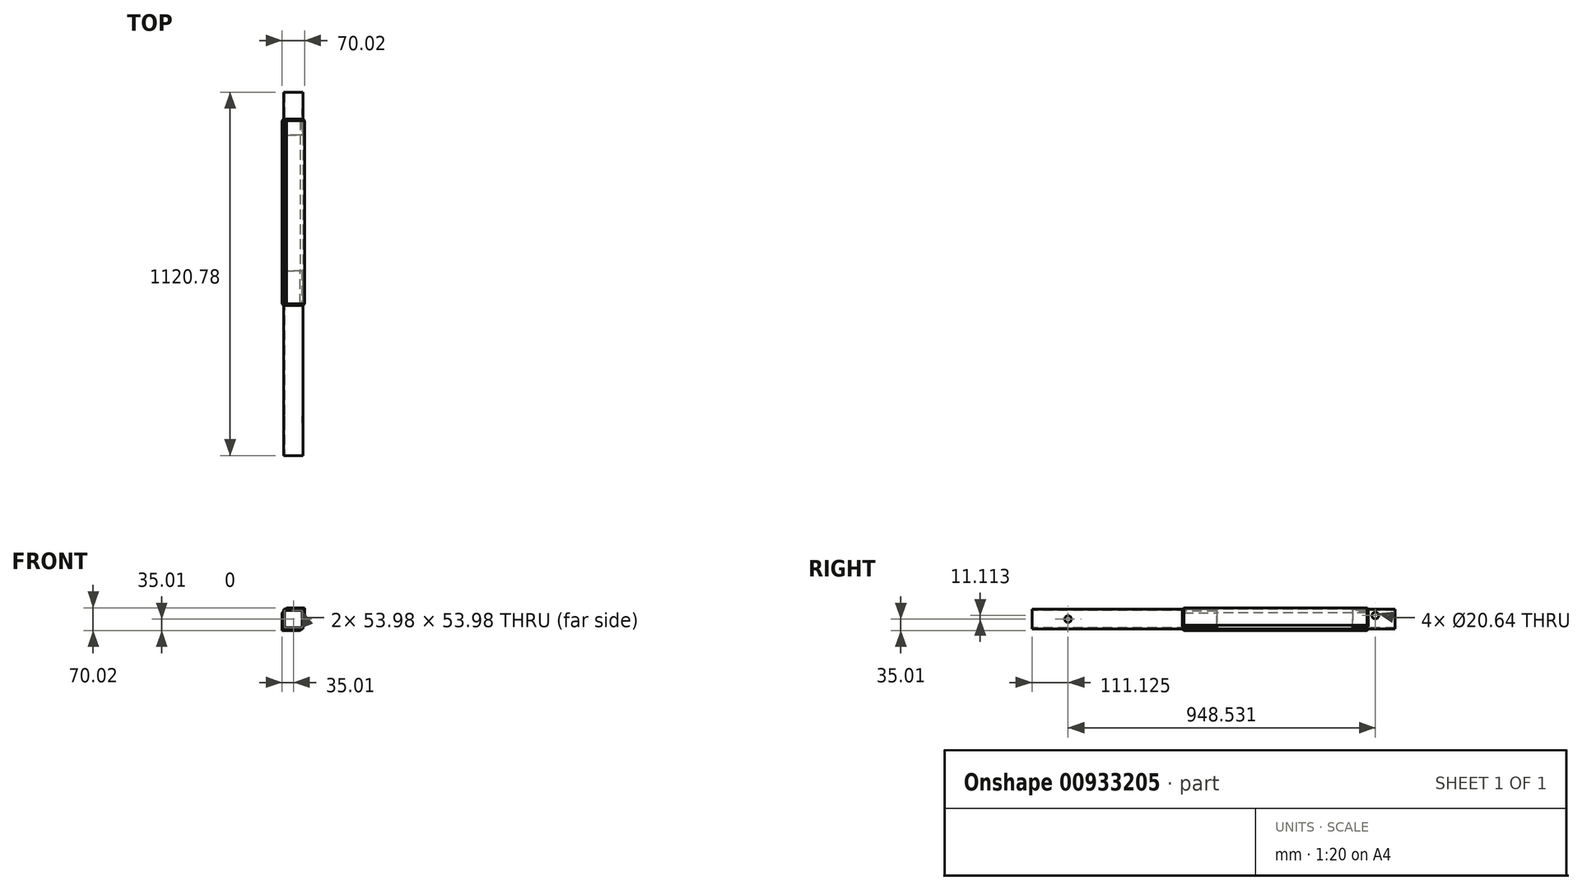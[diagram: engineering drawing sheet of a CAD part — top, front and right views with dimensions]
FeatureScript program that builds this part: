
annotation { "Feature Type Name" : "Feature", "Feature Type Description" : "" }
export const myFeature = defineFeature(function(context is Context, id is Id, definition is map)
    precondition{}
    {
        {
            var Q0;
            Q0=qCreatedBy(makeId("Front.planeOp"),FACE);
            var sketch = newSketch(context, id + "F0", { "sketchPlane" : qUnion([Q0])});
            skLineSegment(sketch, "E0.bottom", {"start": v(26.99, 30.16) * mm, "end": v(-26.99, 30.16) * mm});
            skLineSegment(sketch, "E0.top", {"start": v(26.99, -30.16) * mm, "end": v(-26.99, -30.16) * mm});
            skLineSegment(sketch, "E0.left", {"start": v(30.16, 26.99) * mm, "end": v(30.16, -26.99) * mm});
            skLineSegment(sketch, "E0.right", {"start": v(-30.16, 26.99) * mm, "end": v(-30.16, -26.99) * mm});
            skPoint(sketch, "E0.middle", {"position": v(0, 0) * mm});
            skLineSegment(sketch, "E1.0", {"start": v(23.81, 26.99) * mm, "end": v(-23.81, 26.99) * mm});
            skLineSegment(sketch, "E1.1", {"start": v(26.99, 23.81) * mm, "end": v(26.99, -23.81) * mm});
            skLineSegment(sketch, "E1.2", {"start": v(23.81, -26.99) * mm, "end": v(-23.81, -26.99) * mm});
            skLineSegment(sketch, "E1.3", {"start": v(-26.99, 23.81) * mm, "end": v(-26.99, -23.81) * mm});
            skPoint(sketch, "E2.visualSharp", {"position": v(-26.99, 26.99) * mm});
            skPoint(sketch, "E3.visualSharp", {"position": v(-30.16, 30.16) * mm});
            skPoint(sketch, "E4.visualSharp", {"position": v(30.16, 30.16) * mm});
            skPoint(sketch, "E5.visualSharp", {"position": v(26.99, 26.99) * mm});
            skPoint(sketch, "E6.visualSharp", {"position": v(26.99, -26.99) * mm});
            skPoint(sketch, "E7.visualSharp", {"position": v(30.16, -30.16) * mm});
            skPoint(sketch, "E8.visualSharp", {"position": v(-26.99, -26.99) * mm});
            skPoint(sketch, "E9.visualSharp", {"position": v(-30.16, -30.16) * mm});
            skLineSegment(sketch, "E10", {"start": v(-26.99, -23.81) * mm, "end": v(-26.99, -26.99) * mm});
            skLineSegment(sketch, "E11", {"start": v(-23.81, -26.99) * mm, "end": v(-26.99, -26.99) * mm});
            skLineSegment(sketch, "E12", {"start": v(-30.16, -26.99) * mm, "end": v(-30.16, -30.16) * mm});
            skLineSegment(sketch, "E13", {"start": v(-30.16, -30.16) * mm, "end": v(-26.99, -30.16) * mm});
            skLineSegment(sketch, "E14", {"start": v(26.99, -23.81) * mm, "end": v(26.99, -26.99) * mm});
            skLineSegment(sketch, "E15", {"start": v(26.99, -26.99) * mm, "end": v(23.81, -26.99) * mm});
            skLineSegment(sketch, "E16", {"start": v(30.16, -26.99) * mm, "end": v(30.16, -30.16) * mm});
            skLineSegment(sketch, "E17", {"start": v(26.99, -30.16) * mm, "end": v(30.16, -30.16) * mm});
            skLineSegment(sketch, "E18", {"start": v(26.99, 23.81) * mm, "end": v(26.99, 26.99) * mm});
            skLineSegment(sketch, "E19", {"start": v(26.99, 26.99) * mm, "end": v(23.81, 26.99) * mm});
            skLineSegment(sketch, "E20", {"start": v(30.16, 26.99) * mm, "end": v(30.16, 30.16) * mm});
            skLineSegment(sketch, "E21", {"start": v(26.99, 30.16) * mm, "end": v(30.16, 30.16) * mm});
            skLineSegment(sketch, "E22", {"start": v(-23.81, 26.99) * mm, "end": v(-26.99, 26.99) * mm});
            skLineSegment(sketch, "E23", {"start": v(-26.99, 26.99) * mm, "end": v(-26.99, 23.81) * mm});
            skLineSegment(sketch, "E24", {"start": v(-30.16, 26.99) * mm, "end": v(-30.16, 30.16) * mm});
            skLineSegment(sketch, "E25", {"start": v(-30.16, 30.16) * mm, "end": v(-26.99, 30.16) * mm});
            skSolve(sketch);
        }
        {
            var Q0;
            Q0=makeQuery(id+"F0.imprint","IMPRINT",FACE,{"disambiguationData":[TD([[makeQuery(id+"F0.imprint","IMPRINT",EDGE,{"derivedFrom":sQuery(id+"F0.wireOp",EDGE,"E0.bottom")}),1.0]])]});
            extrude(context, id + "F1", {"entities" : qUnion([Q0]), "oppositeDirection" : true, "depth" : 1120.77 * mm, "offsetDistance" : 25.4 * mm});
        }
        {
            var Q0;
            Q0=qCreatedBy(makeId("Right.planeOp"),FACE);
            var sketch = newSketch(context, id + "F2", { "sketchPlane" : qUnion([Q0])});
            skLineSegment(sketch, "E26", {"start": v(0, 0) * mm, "end": v(569.91, 0) * mm, "construction": true});
            skLineSegment(sketch, "E27", {"start": v(569.91, 0) * mm, "end": v(569.91, -86.32) * mm});
            skLineSegment(sketch, "E28", {"start": v(569.91, -86.32) * mm, "end": v(989.01, -86.32) * mm});
            skLineSegment(sketch, "E29", {"start": v(989.01, -86.32) * mm, "end": v(989.01, 80.05) * mm});
            skLineSegment(sketch, "E30", {"start": v(989.01, 80.05) * mm, "end": v(569.91, 80.05) * mm});
            skLineSegment(sketch, "E31", {"start": v(569.91, 80.05) * mm, "end": v(569.91, 0) * mm});
            skSolve(sketch);
        }
        {
            var Q0;
            Q0 = qSketchRegion(id + "F2", true);
            extrude(context, id + "F3", {"entities" : qUnion([Q0]), "operationType" : NewBodyOperationType.REMOVE, "endBound" : BoundingType.SYMMETRIC, "oppositeDirection" : true, "depth" : 106.68 * mm, "offsetDistance" : 25.4 * mm});
        }
        {
            var Q0;
            Q0=qCreatedBy(makeId("Front.planeOp"),FACE);
            cPlane(context, id + "F4", {"entities" : qUnion([Q0]), "cplaneType" : CPlaneType.OFFSET, "offset" : 468.3 * mm, "oppositeDirection" : true, "width" : 152.4 * mm, "height" : 152.4 * mm});
        }
        {
            var Q0;
            Q0=qCreatedBy(id+"F4.planeOp",FACE);
            var sketch = newSketch(context, id + "F5", { "sketchPlane" : qUnion([Q0])});
            skLineSegment(sketch, "E32", {"start": v(0, 0) * mm, "end": v(0, 30.25) * mm, "construction": true});
            skLineSegment(sketch, "E33", {"start": v(0, 0) * mm, "end": v(30.25, 0) * mm, "construction": true});
            skLineSegment(sketch, "E34", {"start": v(30.25, 0) * mm, "end": v(-20.55, 0) * mm, "construction": true});
            skLineSegment(sketch, "E35", {"start": v(-20.55, 0) * mm, "end": v(-20.55, 30.25) * mm, "construction": true});
            skLineSegment(sketch, "E36", {"start": v(-20.55, 30.25) * mm, "end": v(30.25, 30.25) * mm});
            skLineSegment(sketch, "E37", {"start": v(30.25, 30.25) * mm, "end": v(30.25, -19.03) * mm});
            skLineSegment(sketch, "E38", {"start": v(30.25, -19.03) * mm, "end": v(35.01, -19.03) * mm});
            skLineSegment(sketch, "E39", {"start": v(35.01, -19.03) * mm, "end": v(35.01, 35.01) * mm});
            skLineSegment(sketch, "E40", {"start": v(35.01, 35.01) * mm, "end": v(-20.55, 35.01) * mm});
            skLineSegment(sketch, "E41", {"start": v(-20.55, 35.01) * mm, "end": v(-20.55, 30.25) * mm});
            skLineSegment(sketch, "E42.1.0", {"start": v(-35.01, 19.03) * mm, "end": v(-35.01, -35.01) * mm});
            skLineSegment(sketch, "E42.1.1", {"start": v(-35.01, -35.01) * mm, "end": v(20.55, -35.01) * mm});
            skLineSegment(sketch, "E42.1.2", {"start": v(20.55, -35.01) * mm, "end": v(20.55, -30.25) * mm});
            skLineSegment(sketch, "E42.1.3", {"start": v(20.55, -30.25) * mm, "end": v(-30.25, -30.25) * mm});
            skLineSegment(sketch, "E42.1.4", {"start": v(-30.25, -30.25) * mm, "end": v(-30.25, 19.03) * mm});
            skLineSegment(sketch, "E42.1.5", {"start": v(-30.25, 19.03) * mm, "end": v(-35.01, 19.03) * mm});
            skPoint(sketch, "E42.center", {"position": v(0, 0) * mm});
            skSolve(sketch);
        }
        {
            var Q0;
            Q0=makeQuery(id+"F5.imprint","IMPRINT",FACE,{"disambiguationData":[TD([[makeQuery(id+"F5.imprint","IMPRINT",EDGE,{"derivedFrom":sQuery(id+"F5.wireOp",EDGE,"E36")}),1.0]])]});
            var Q1;
            Q1=makeQuery(id+"F5.imprint","IMPRINT",FACE,{"disambiguationData":[TD([[makeQuery(id+"F5.imprint","IMPRINT",EDGE,{"derivedFrom":sQuery(id+"F5.wireOp",EDGE,"E42.1.0")}),1.0]])]});
            extrude(context, id + "F6", {"entities" : qUnion([Q0, Q1]), "oppositeDirection" : true, "depth" : 565.15 * mm, "offsetDistance" : 25.4 * mm});
        }
        {
            var Q0;
            Q0=makeQuery(id+"F6.opExtrude","SWEPT_FACE",FACE,{"disambiguationData":[OSD([sQuery(id+"F5.wireOp",EDGE,"E41")])]});
            var sketch = newSketch(context, id + "F7", { "sketchPlane" : qUnion([Q0])});
            skLineSegment(sketch, "E43", {"start": v(-468.31, 35.01) * mm, "end": v(-459.42, 26.12) * mm});
            skLineSegment(sketch, "E44", {"start": v(-459.42, 26.12) * mm, "end": v(-468.31, 26.12) * mm});
            skLineSegment(sketch, "E45", {"start": v(-468.31, 26.12) * mm, "end": v(-468.31, 35.01) * mm});
            skLineSegment(sketch, "E46", {"start": v(-1033.46, 35.01) * mm, "end": v(-1033.46, 26.12) * mm});
            skLineSegment(sketch, "E47", {"start": v(-1033.46, 26.12) * mm, "end": v(-1042.35, 26.12) * mm});
            skLineSegment(sketch, "E48", {"start": v(-1042.35, 26.12) * mm, "end": v(-1033.46, 35.01) * mm});
            skSolve(sketch);
        }
        {
            var Q0;
            {var subQ4=sQuery(id+"F7.wireOp",EDGE,"E47");Q0=makeQuery(id+"F7.imprint","IMPRINT",FACE,{"disambiguationData":[TD([[makeQuery(id+"F7.imprint","IMPRINT",EDGE,{"derivedFrom":subQ4}),-1.0]])]});}
            var Q1;
            {var subQ0=sQuery(id+"F7.wireOp",EDGE,"E43");Q1=makeQuery(id+"F7.imprint","IMPRINT",FACE,{"disambiguationData":[TD([[makeQuery(id+"F7.imprint","IMPRINT",EDGE,{"derivedFrom":subQ0}),-1.0]])]});}
            var Q2;
            Q2=makeQuery(id+"F6.opExtrude","SWEPT_FACE",FACE,{"disambiguationData":[OSD([sQuery(id+"F5.wireOp",EDGE,"E39")])]});
            extrude(context, id + "F8", {"entities" : qUnion([Q0, Q1]), "operationType" : NewBodyOperationType.ADD, "endBound" : BoundingType.UP_TO_SURFACE, "oppositeDirection" : true, "depth" : 50.8 * mm, "endBoundEntityFace" : qUnion([Q2]), "offsetDistance" : 25.4 * mm});
        }
        {
            var Q0;
            Q0=makeQuery(id+"F6.opExtrude","SWEPT_FACE",FACE,{"disambiguationData":[OSD([sQuery(id+"F5.wireOp",EDGE,"E38")])]});
            var sketch = newSketch(context, id + "F9", { "sketchPlane" : qUnion([Q0])});
            skLineSegment(sketch, "E49", {"start": v(35.01, -1033.46) * mm, "end": v(26.12, -1033.46) * mm});
            skLineSegment(sketch, "E50", {"start": v(26.12, -1033.46) * mm, "end": v(26.12, -1042.35) * mm});
            skLineSegment(sketch, "E51", {"start": v(26.12, -1042.35) * mm, "end": v(35.01, -1033.46) * mm});
            skLineSegment(sketch, "E52", {"start": v(35.01, -468.31) * mm, "end": v(26.12, -468.31) * mm});
            skLineSegment(sketch, "E53", {"start": v(26.12, -468.31) * mm, "end": v(26.12, -459.42) * mm});
            skLineSegment(sketch, "E54", {"start": v(26.12, -459.42) * mm, "end": v(35.01, -468.31) * mm});
            skSolve(sketch);
        }
        {
            var Q0;
            {var subQ4=sQuery(id+"F9.wireOp",EDGE,"E53");Q0=makeQuery(id+"F9.imprint","IMPRINT",FACE,{"disambiguationData":[TD([[makeQuery(id+"F9.imprint","IMPRINT",EDGE,{"derivedFrom":subQ4}),-1.0]])]});}
            var Q1;
            {var subQ4=sQuery(id+"F9.wireOp",EDGE,"E50");Q1=makeQuery(id+"F9.imprint","IMPRINT",FACE,{"disambiguationData":[TD([[makeQuery(id+"F9.imprint","IMPRINT",EDGE,{"derivedFrom":subQ4}),1.0]])]});}
            var Q2;
            Q2=makeQuery(id+"F8.opExtrude","SWEPT_FACE",FACE,{"disambiguationData":[OSD([sQuery(id+"F7.wireOp",EDGE,"E47")])]});
            extrude(context, id + "F10", {"entities" : qUnion([Q0, Q1]), "operationType" : NewBodyOperationType.ADD, "endBound" : BoundingType.UP_TO_SURFACE, "oppositeDirection" : true, "depth" : 25.4 * mm, "endBoundEntityFace" : qUnion([Q2]), "offsetDistance" : 25.4 * mm});
        }
        {
            var Q0;
            {var subQ3=sQuery(id+"F7.wireOp",EDGE,"E44");Q0=makeQuery(id+"F8.boolean.opBoolean","SPLIT",FACE,{"disambiguationData":[TD([makeQuery(id+"F1.opExtrude","SWEPT_FACE",FACE,{"disambiguationData":[OSD([sQuery(id+"F0.wireOp",EDGE,"E0.left")])]})])],"derivedFrom":makeQuery(id+"F8.opExtrude","SWEPT_FACE",FACE,{"disambiguationData":[OSD([subQ3])]})});}
            var sketch = newSketch(context, id + "F11", { "sketchPlane" : qUnion([Q0])});
            skLineSegment(sketch, "E55", {"start": v(30.16, -459.42) * mm, "end": v(35.01, -459.42) * mm});
            skLineSegment(sketch, "E56", {"start": v(35.01, -459.42) * mm, "end": v(35.01, -468.31) * mm});
            skLineSegment(sketch, "E57", {"start": v(35.01, -468.31) * mm, "end": v(30.16, -463.46) * mm});
            skLineSegment(sketch, "E58", {"start": v(30.16, -463.46) * mm, "end": v(30.16, -459.42) * mm});
            skSolve(sketch);
        }
        {
            var Q0;
            Q0 = qSketchRegion(id + "F11", true);
            extrude(context, id + "F12", {"entities" : qUnion([Q0]), "operationType" : NewBodyOperationType.REMOVE, "oppositeDirection" : true, "depth" : 25.4 * mm, "offsetDistance" : 25.4 * mm});
        }
        {
            var Q0;
            {var subQ1=sQuery(id+"F5.wireOp",EDGE,"E37");var subQ4=sQuery(id+"F7.wireOp",EDGE,"E47");Q0=makeQuery(id+"F8.boolean.opBoolean","SPLIT",FACE,{"disambiguationData":[TD([makeQuery(id+"F6.opExtrude","SWEPT_FACE",FACE,{"disambiguationData":[OSD([subQ1])]})])],"derivedFrom":makeQuery(id+"F8.opExtrude","SWEPT_FACE",FACE,{"disambiguationData":[OSD([subQ4])]})});}
            var sketch = newSketch(context, id + "F13", { "sketchPlane" : qUnion([Q0])});
            skLineSegment(sketch, "E59", {"start": v(35.01, -1033.46) * mm, "end": v(30.16, -1038.31) * mm});
            skLineSegment(sketch, "E60", {"start": v(30.16, -1038.31) * mm, "end": v(30.16, -1042.35) * mm});
            skLineSegment(sketch, "E61", {"start": v(30.16, -1042.35) * mm, "end": v(35.01, -1042.35) * mm});
            skLineSegment(sketch, "E62", {"start": v(35.01, -1042.35) * mm, "end": v(35.01, -1033.46) * mm});
            skSolve(sketch);
        }
        {
            var Q0;
            Q0 = qSketchRegion(id + "F13", true);
            extrude(context, id + "F14", {"entities" : qUnion([Q0]), "operationType" : NewBodyOperationType.REMOVE, "oppositeDirection" : true, "depth" : 25.4 * mm, "offsetDistance" : 25.4 * mm});
        }
        {
            var Q0;
            Q0=makeQuery(id+"F6.opExtrude","SWEPT_FACE",FACE,{"disambiguationData":[OSD([sQuery(id+"F5.wireOp",EDGE,"E42.1.2")])]});
            var sketch = newSketch(context, id + "F15", { "sketchPlane" : qUnion([Q0])});
            skLineSegment(sketch, "E63", {"start": v(468.31, -35.01) * mm, "end": v(468.31, -26.12) * mm});
            skLineSegment(sketch, "E64", {"start": v(468.31, -26.12) * mm, "end": v(459.42, -26.12) * mm});
            skLineSegment(sketch, "E65", {"start": v(459.42, -26.12) * mm, "end": v(468.31, -35.01) * mm});
            skLineSegment(sketch, "E66", {"start": v(1033.46, -35.01) * mm, "end": v(1033.46, -26.12) * mm});
            skLineSegment(sketch, "E67", {"start": v(1033.46, -26.12) * mm, "end": v(1042.35, -26.12) * mm});
            skLineSegment(sketch, "E68", {"start": v(1042.35, -26.12) * mm, "end": v(1033.46, -35.01) * mm});
            skSolve(sketch);
        }
        {
            var Q0;
            Q0 = qSketchRegion(id + "F15", true);
            var Q1;
            Q1=makeQuery(id+"F6.opExtrude","SWEPT_FACE",FACE,{"disambiguationData":[OSD([sQuery(id+"F5.wireOp",EDGE,"E42.1.0")])]});
            extrude(context, id + "F16", {"entities" : qUnion([Q0]), "operationType" : NewBodyOperationType.ADD, "endBound" : BoundingType.UP_TO_SURFACE, "oppositeDirection" : true, "depth" : 25.4 * mm, "endBoundEntityFace" : qUnion([Q1]), "offsetDistance" : 25.4 * mm});
        }
        {
            var Q0;
            Q0=makeQuery(id+"F6.opExtrude","SWEPT_FACE",FACE,{"disambiguationData":[OSD([sQuery(id+"F5.wireOp",EDGE,"E42.1.5")])]});
            var sketch = newSketch(context, id + "F17", { "sketchPlane" : qUnion([Q0])});
            skLineSegment(sketch, "E69", {"start": v(-35.01, 468.31) * mm, "end": v(-26.12, 468.31) * mm});
            skLineSegment(sketch, "E70", {"start": v(-26.12, 468.31) * mm, "end": v(-26.12, 459.42) * mm});
            skLineSegment(sketch, "E71", {"start": v(-26.12, 459.42) * mm, "end": v(-35.01, 468.31) * mm});
            skLineSegment(sketch, "E72", {"start": v(-35.01, 1033.46) * mm, "end": v(-26.12, 1033.46) * mm});
            skLineSegment(sketch, "E73", {"start": v(-26.12, 1033.46) * mm, "end": v(-26.12, 1042.35) * mm});
            skLineSegment(sketch, "E74", {"start": v(-26.12, 1042.35) * mm, "end": v(-35.01, 1033.46) * mm});
            skSolve(sketch);
        }
        {
            var Q0;
            Q0 = qSketchRegion(id + "F17", true);
            var Q1;
            {var subQ2=sQuery(id+"F0.wireOp",EDGE,"E17");var subQ4=sQuery(id+"F0.wireOp",EDGE,"E13");var subQ8=sQuery(id+"F0.wireOp",EDGE,"E0.top");Q1=makeQuery(id+"F3.boolean.opBoolean","SPLIT",FACE,{"disambiguationData":[TD([makeQuery(id+"F3.opExtrude","SWEPT_FACE",FACE,{"disambiguationData":[OSD([sQuery(id+"F2.wireOp",EDGE,"E27"),sQuery(id+"F2.wireOp",EDGE,"E31")])]})])],"derivedFrom":makeQuery(id+"F1.opExtrude","SWEPT_FACE",FACE,{"disambiguationData":[OSD([subQ8,subQ4,subQ2])]})});}
            extrude(context, id + "F18", {"entities" : qUnion([Q0]), "operationType" : NewBodyOperationType.ADD, "endBound" : BoundingType.UP_TO_SURFACE, "oppositeDirection" : true, "depth" : 50.8 * mm, "endBoundEntityFace" : qUnion([Q1]), "offsetDistance" : 25.4 * mm});
        }
        {
            var Q0;
            {var subQ1=sQuery(id+"F5.wireOp",EDGE,"E42.1.0");var subQ3=sQuery(id+"F15.wireOp",EDGE,"E67");Q0=makeQuery(id+"F16.boolean.opBoolean","SPLIT",FACE,{"disambiguationData":[TD([makeQuery(id+"F6.opExtrude","SWEPT_FACE",FACE,{"disambiguationData":[OSD([subQ1])]})])],"derivedFrom":makeQuery(id+"F16.opExtrude","SWEPT_FACE",FACE,{"disambiguationData":[OSD([subQ3])]})});}
            var sketch = newSketch(context, id + "F19", { "sketchPlane" : qUnion([Q0])});
            skLineSegment(sketch, "E75", {"start": v(-30.16, 1038.31) * mm, "end": v(-30.16, 1042.35) * mm});
            skLineSegment(sketch, "E76", {"start": v(-30.16, 1042.35) * mm, "end": v(-35.01, 1042.35) * mm});
            skLineSegment(sketch, "E77", {"start": v(-35.01, 1042.35) * mm, "end": v(-35.01, 1033.46) * mm});
            skLineSegment(sketch, "E78", {"start": v(-35.01, 1033.46) * mm, "end": v(-30.16, 1038.31) * mm});
            skSolve(sketch);
        }
        {
            var Q0;
            Q0 = qSketchRegion(id + "F19", true);
            extrude(context, id + "F20", {"entities" : qUnion([Q0]), "operationType" : NewBodyOperationType.REMOVE, "oppositeDirection" : true, "depth" : 25.4 * mm, "offsetDistance" : 25.4 * mm});
        }
        {
            var Q0;
            Q0=makeQuery(id+"F3.boolean.opBoolean","COPY",FACE,{"derivedFrom":makeQuery(id+"F3.opExtrude","SWEPT_FACE",FACE,{"disambiguationData":[OSD([sQuery(id+"F2.wireOp",EDGE,"E27"),sQuery(id+"F2.wireOp",EDGE,"E31")])]})});
            var sketch = newSketch(context, id + "F21", { "sketchPlane" : qUnion([Q0])});
            skLineSegment(sketch, "E79", {"start": v(20.55, 35.01) * mm, "end": v(20.55, 26.12) * mm});
            skLineSegment(sketch, "E80", {"start": v(20.55, 26.12) * mm, "end": v(29.44, 26.12) * mm});
            skLineSegment(sketch, "E81", {"start": v(29.44, 26.12) * mm, "end": v(20.55, 35.01) * mm});
            skLineSegment(sketch, "E82", {"start": v(26.12, 27.92) * mm, "end": v(26.12, 19.03) * mm});
            skLineSegment(sketch, "E83", {"start": v(26.12, 19.03) * mm, "end": v(35.01, 19.03) * mm});
            skLineSegment(sketch, "E84", {"start": v(35.01, 19.03) * mm, "end": v(26.12, 27.92) * mm});
            skLineSegment(sketch, "E85", {"start": v(-26.12, -19.03) * mm, "end": v(-26.12, -27.92) * mm});
            skLineSegment(sketch, "E86", {"start": v(-26.12, -19.03) * mm, "end": v(-35.01, -19.03) * mm});
            skLineSegment(sketch, "E87", {"start": v(-35.01, -19.03) * mm, "end": v(-26.12, -27.92) * mm});
            skLineSegment(sketch, "E88", {"start": v(-20.55, -26.12) * mm, "end": v(-20.55, -35.01) * mm});
            skLineSegment(sketch, "E89", {"start": v(-20.55, -35.01) * mm, "end": v(-29.44, -26.12) * mm});
            skLineSegment(sketch, "E90", {"start": v(-29.44, -26.12) * mm, "end": v(-20.55, -26.12) * mm});
            skSolve(sketch);
        }
        {
            var Q0;
            Q0 = qSketchRegion(id + "F21", true);
            extrude(context, id + "F22", {"entities" : qUnion([Q0]), "operationType" : NewBodyOperationType.ADD, "oppositeDirection" : true, "depth" : 113.8 * mm, "offsetDistance" : 25.4 * mm});
        }
        {
            var Q0;
            {var subQ0=sQuery(id+"F21.wireOp",EDGE,"E89");var subQ1=sQuery(id+"F21.wireOp",EDGE,"E88");Q0=makeQuery(id+"F22.boolean.opBoolean","SPLIT",FACE,{"disambiguationData":[TD([makeQuery(id+"F1.opExtrude","SWEPT_FACE",FACE,{"disambiguationData":[OSD([sQuery(id+"F0.wireOp",EDGE,"E0.top"),sQuery(id+"F0.wireOp",EDGE,"E13"),sQuery(id+"F0.wireOp",EDGE,"E17")])]}),makeQuery(id+"F6.opExtrude","SWEPT_FACE",FACE,{"disambiguationData":[OSD([sQuery(id+"F5.wireOp",EDGE,"E42.1.1")])]}),makeQuery(id+"F16.opExtrude","SWEPT_FACE",FACE,{"disambiguationData":[OSD([sQuery(id+"F15.wireOp",EDGE,"E65")])]}),makeQuery(id+"F22.opExtrude","CAP_FACE",FACE,{"disambiguationData":[OSD([sQuery(id+"F21.wireOp",EDGE,"E85"),sQuery(id+"F21.wireOp",EDGE,"E86"),sQuery(id+"F21.wireOp",EDGE,"E87"),subQ1,subQ0,sQuery(id+"F21.wireOp",EDGE,"E90")])],"isStart":false}),makeQuery(id+"F22.opExtrude","SWEPT_FACE",FACE,{"disambiguationData":[OSD([subQ0])]})])],"derivedFrom":makeQuery(id+"F22.opExtrude","SWEPT_FACE",FACE,{"disambiguationData":[OSD([subQ1])]})});}
            var sketch = newSketch(context, id + "F23", { "sketchPlane" : qUnion([Q0])});
            skLineSegment(sketch, "E91", {"start": v(-456.12, -35.01) * mm, "end": v(-468.31, -35.01) * mm});
            skLineSegment(sketch, "E92", {"start": v(-468.31, -35.01) * mm, "end": v(-463.46, -30.16) * mm});
            skLineSegment(sketch, "E93", {"start": v(-463.46, -30.16) * mm, "end": v(-456.12, -30.16) * mm});
            skLineSegment(sketch, "E94", {"start": v(-456.12, -30.16) * mm, "end": v(-456.12, -35.01) * mm});
            skSolve(sketch);
        }
        {
            var Q0;
            Q0 = qSketchRegion(id + "F23", true);
            extrude(context, id + "F24", {"entities" : qUnion([Q0]), "operationType" : NewBodyOperationType.REMOVE, "oppositeDirection" : true, "depth" : 25.4 * mm, "offsetDistance" : 25.4 * mm});
        }
        {
            var Q0;
            {var subQ0=sQuery(id+"F21.wireOp",EDGE,"E87");var subQ1=sQuery(id+"F21.wireOp",EDGE,"E86");Q0=makeQuery(id+"F22.boolean.opBoolean","SPLIT",FACE,{"disambiguationData":[TD([makeQuery(id+"F1.opExtrude","SWEPT_FACE",FACE,{"disambiguationData":[OSD([sQuery(id+"F0.wireOp",EDGE,"E0.left"),sQuery(id+"F0.wireOp",EDGE,"E16"),sQuery(id+"F0.wireOp",EDGE,"E20")])]}),makeQuery(id+"F6.opExtrude","SWEPT_FACE",FACE,{"disambiguationData":[OSD([sQuery(id+"F5.wireOp",EDGE,"E39")])]}),makeQuery(id+"F8.opExtrude","CAP_FACE",FACE,{"disambiguationData":[OSD([sQuery(id+"F7.wireOp",EDGE,"E43"),sQuery(id+"F7.wireOp",EDGE,"E44"),sQuery(id+"F7.wireOp",EDGE,"E45")])],"isStart":false}),makeQuery(id+"F8.opExtrude","CAP_FACE",FACE,{"disambiguationData":[OSD([sQuery(id+"F7.wireOp",EDGE,"E46"),sQuery(id+"F7.wireOp",EDGE,"E47"),sQuery(id+"F7.wireOp",EDGE,"E48")])],"isStart":false}),makeQuery(id+"F10.opExtrude","SWEPT_FACE",FACE,{"disambiguationData":[OSD([sQuery(id+"F9.wireOp",EDGE,"E54")])]}),makeQuery(id+"F22.opExtrude","CAP_FACE",FACE,{"disambiguationData":[OSD([sQuery(id+"F21.wireOp",EDGE,"E85"),subQ1,subQ0,sQuery(id+"F21.wireOp",EDGE,"E88"),sQuery(id+"F21.wireOp",EDGE,"E89"),sQuery(id+"F21.wireOp",EDGE,"E90")])],"isStart":false}),makeQuery(id+"F22.opExtrude","SWEPT_FACE",FACE,{"disambiguationData":[OSD([subQ0])]})])],"derivedFrom":makeQuery(id+"F22.opExtrude","SWEPT_FACE",FACE,{"disambiguationData":[OSD([subQ1])]})});}
            var sketch = newSketch(context, id + "F25", { "sketchPlane" : qUnion([Q0])});
            skLineSegment(sketch, "E95", {"start": v(30.16, 463.46) * mm, "end": v(30.16, 456.12) * mm});
            skLineSegment(sketch, "E96", {"start": v(30.16, 456.12) * mm, "end": v(35.01, 456.12) * mm});
            skLineSegment(sketch, "E97", {"start": v(35.01, 456.12) * mm, "end": v(35.01, 468.31) * mm});
            skLineSegment(sketch, "E98", {"start": v(35.01, 468.31) * mm, "end": v(30.16, 463.46) * mm});
            skSolve(sketch);
        }
        {
            var Q0;
            Q0 = qSketchRegion(id + "F25", true);
            extrude(context, id + "F26", {"entities" : qUnion([Q0]), "operationType" : NewBodyOperationType.REMOVE, "oppositeDirection" : true, "depth" : 25.4 * mm, "offsetDistance" : 25.4 * mm});
        }
        {
            var Q0;
            {var subQ0=sQuery(id+"F21.wireOp",EDGE,"E81");var subQ1=sQuery(id+"F21.wireOp",EDGE,"E79");Q0=makeQuery(id+"F22.boolean.opBoolean","SPLIT",FACE,{"disambiguationData":[TD([makeQuery(id+"F1.opExtrude","SWEPT_FACE",FACE,{"disambiguationData":[OSD([sQuery(id+"F0.wireOp",EDGE,"E0.bottom"),sQuery(id+"F0.wireOp",EDGE,"E21"),sQuery(id+"F0.wireOp",EDGE,"E25")])]}),makeQuery(id+"F6.opExtrude","SWEPT_FACE",FACE,{"disambiguationData":[OSD([sQuery(id+"F5.wireOp",EDGE,"E40")])]}),makeQuery(id+"F8.opExtrude","SWEPT_FACE",FACE,{"disambiguationData":[OSD([sQuery(id+"F7.wireOp",EDGE,"E43")])]}),makeQuery(id+"F22.opExtrude","CAP_FACE",FACE,{"disambiguationData":[OSD([subQ1,sQuery(id+"F21.wireOp",EDGE,"E80"),subQ0,sQuery(id+"F21.wireOp",EDGE,"E82"),sQuery(id+"F21.wireOp",EDGE,"E83"),sQuery(id+"F21.wireOp",EDGE,"E84")])],"isStart":false}),makeQuery(id+"F22.opExtrude","SWEPT_FACE",FACE,{"disambiguationData":[OSD([subQ0])]})])],"derivedFrom":makeQuery(id+"F22.opExtrude","SWEPT_FACE",FACE,{"disambiguationData":[OSD([subQ1])]})});}
            var sketch = newSketch(context, id + "F27", { "sketchPlane" : qUnion([Q0])});
            skLineSegment(sketch, "E99", {"start": v(456.12, 30.16) * mm, "end": v(456.12, 35.01) * mm});
            skLineSegment(sketch, "E100", {"start": v(456.12, 35.01) * mm, "end": v(468.31, 35.01) * mm});
            skLineSegment(sketch, "E101", {"start": v(468.31, 35.01) * mm, "end": v(463.46, 30.16) * mm});
            skLineSegment(sketch, "E102", {"start": v(463.46, 30.16) * mm, "end": v(456.12, 30.16) * mm});
            skSolve(sketch);
        }
        {
            var Q0;
            Q0 = qSketchRegion(id + "F27", true);
            extrude(context, id + "F28", {"entities" : qUnion([Q0]), "operationType" : NewBodyOperationType.REMOVE, "oppositeDirection" : true, "depth" : 25.4 * mm, "offsetDistance" : 25.4 * mm});
        }
        {
            var Q0;
            {var subQ0=sQuery(id+"F21.wireOp",EDGE,"E84");var subQ1=sQuery(id+"F21.wireOp",EDGE,"E83");Q0=makeQuery(id+"F22.boolean.opBoolean","SPLIT",FACE,{"disambiguationData":[TD([makeQuery(id+"F1.opExtrude","SWEPT_FACE",FACE,{"disambiguationData":[OSD([sQuery(id+"F0.wireOp",EDGE,"E0.right"),sQuery(id+"F0.wireOp",EDGE,"E12"),sQuery(id+"F0.wireOp",EDGE,"E24")])]}),makeQuery(id+"F6.opExtrude","SWEPT_FACE",FACE,{"disambiguationData":[OSD([sQuery(id+"F5.wireOp",EDGE,"E42.1.0")])]}),makeQuery(id+"F16.opExtrude","CAP_FACE",FACE,{"disambiguationData":[OSD([sQuery(id+"F15.wireOp",EDGE,"E63"),sQuery(id+"F15.wireOp",EDGE,"E64"),sQuery(id+"F15.wireOp",EDGE,"E65")])],"isStart":false}),makeQuery(id+"F16.opExtrude","CAP_FACE",FACE,{"disambiguationData":[OSD([sQuery(id+"F15.wireOp",EDGE,"E66"),sQuery(id+"F15.wireOp",EDGE,"E67"),sQuery(id+"F15.wireOp",EDGE,"E68")])],"isStart":false}),makeQuery(id+"F18.opExtrude","SWEPT_FACE",FACE,{"disambiguationData":[OSD([sQuery(id+"F17.wireOp",EDGE,"E71")])]}),makeQuery(id+"F22.opExtrude","CAP_FACE",FACE,{"disambiguationData":[OSD([sQuery(id+"F21.wireOp",EDGE,"E79"),sQuery(id+"F21.wireOp",EDGE,"E80"),sQuery(id+"F21.wireOp",EDGE,"E81"),sQuery(id+"F21.wireOp",EDGE,"E82"),subQ1,subQ0])],"isStart":false}),makeQuery(id+"F22.opExtrude","SWEPT_FACE",FACE,{"disambiguationData":[OSD([subQ0])]})])],"derivedFrom":makeQuery(id+"F22.opExtrude","SWEPT_FACE",FACE,{"disambiguationData":[OSD([subQ1])]})});}
            var sketch = newSketch(context, id + "F29", { "sketchPlane" : qUnion([Q0])});
            skLineSegment(sketch, "E103", {"start": v(-30.16, -463.46) * mm, "end": v(-30.16, -456.12) * mm});
            skLineSegment(sketch, "E104", {"start": v(-30.16, -456.12) * mm, "end": v(-35.01, -456.12) * mm});
            skLineSegment(sketch, "E105", {"start": v(-35.01, -456.12) * mm, "end": v(-35.01, -468.31) * mm});
            skLineSegment(sketch, "E106", {"start": v(-35.01, -468.31) * mm, "end": v(-30.16, -463.46) * mm});
            skSolve(sketch);
        }
        {
            var Q0;
            Q0 = qSketchRegion(id + "F29", true);
            extrude(context, id + "F30", {"entities" : qUnion([Q0]), "operationType" : NewBodyOperationType.REMOVE, "endBound" : BoundingType.SYMMETRIC, "oppositeDirection" : true, "depth" : 508 * mm, "offsetDistance" : 25.4 * mm});
        }
        {
            var Q0;
            Q0=makeQuery(id+"F3.boolean.opBoolean","COPY",FACE,{"derivedFrom":makeQuery(id+"F3.opExtrude","SWEPT_FACE",FACE,{"disambiguationData":[OSD([sQuery(id+"F2.wireOp",EDGE,"E29")])]})});
            var sketch = newSketch(context, id + "F31", { "sketchPlane" : qUnion([Q0])});
            skLineSegment(sketch, "E107", {"start": v(-26.12, 19.03) * mm, "end": v(-35.01, 19.03) * mm});
            skLineSegment(sketch, "E108", {"start": v(-26.12, 19.03) * mm, "end": v(-26.12, 27.92) * mm});
            skLineSegment(sketch, "E109", {"start": v(-26.12, 27.92) * mm, "end": v(-35.01, 19.03) * mm});
            skLineSegment(sketch, "E110", {"start": v(-20.55, 26.12) * mm, "end": v(-29.44, 26.12) * mm});
            skLineSegment(sketch, "E111", {"start": v(-20.55, 26.12) * mm, "end": v(-20.55, 35.01) * mm});
            skLineSegment(sketch, "E112", {"start": v(-20.55, 35.01) * mm, "end": v(-29.44, 26.12) * mm});
            skLineSegment(sketch, "E113", {"start": v(20.55, -35.01) * mm, "end": v(20.55, -26.12) * mm});
            skLineSegment(sketch, "E114", {"start": v(20.55, -26.12) * mm, "end": v(29.44, -26.12) * mm});
            skLineSegment(sketch, "E115", {"start": v(29.44, -26.12) * mm, "end": v(20.55, -35.01) * mm});
            skLineSegment(sketch, "E116", {"start": v(26.12, -19.03) * mm, "end": v(26.12, -27.92) * mm});
            skLineSegment(sketch, "E117", {"start": v(26.12, -19.03) * mm, "end": v(35.01, -19.03) * mm});
            skLineSegment(sketch, "E118", {"start": v(35.01, -19.03) * mm, "end": v(26.12, -27.92) * mm});
            skSolve(sketch);
        }
        {
            var Q0;
            Q0 = qSketchRegion(id + "F31", true);
            extrude(context, id + "F32", {"entities" : qUnion([Q0]), "operationType" : NewBodyOperationType.ADD, "oppositeDirection" : true, "depth" : 63.5 * mm, "offsetDistance" : 25.4 * mm});
        }
        {
            var Q0;
            {var subQ0=sQuery(id+"F31.wireOp",EDGE,"E115");var subQ1=sQuery(id+"F31.wireOp",EDGE,"E113");Q0=makeQuery(id+"F32.boolean.opBoolean","SPLIT",FACE,{"disambiguationData":[TD([makeQuery(id+"F1.opExtrude","SWEPT_FACE",FACE,{"disambiguationData":[OSD([sQuery(id+"F0.wireOp",EDGE,"E0.top"),sQuery(id+"F0.wireOp",EDGE,"E13"),sQuery(id+"F0.wireOp",EDGE,"E17")])]}),makeQuery(id+"F6.opExtrude","SWEPT_FACE",FACE,{"disambiguationData":[OSD([sQuery(id+"F5.wireOp",EDGE,"E42.1.1")])]}),makeQuery(id+"F16.opExtrude","SWEPT_FACE",FACE,{"disambiguationData":[OSD([sQuery(id+"F15.wireOp",EDGE,"E68")])]}),makeQuery(id+"F32.opExtrude","CAP_FACE",FACE,{"disambiguationData":[OSD([subQ1,sQuery(id+"F31.wireOp",EDGE,"E114"),subQ0,sQuery(id+"F31.wireOp",EDGE,"E116"),sQuery(id+"F31.wireOp",EDGE,"E117"),sQuery(id+"F31.wireOp",EDGE,"E118")])],"isStart":false}),makeQuery(id+"F32.opExtrude","SWEPT_FACE",FACE,{"disambiguationData":[OSD([subQ0])]})])],"derivedFrom":makeQuery(id+"F32.opExtrude","SWEPT_FACE",FACE,{"disambiguationData":[OSD([subQ1])]})});}
            var sketch = newSketch(context, id + "F33", { "sketchPlane" : qUnion([Q0])});
            skLineSegment(sketch, "E119", {"start": v(-1033.46, -35.01) * mm, "end": v(-1038.31, -30.16) * mm});
            skLineSegment(sketch, "E120", {"start": v(-1038.31, -30.16) * mm, "end": v(-1052.51, -30.16) * mm});
            skLineSegment(sketch, "E121", {"start": v(-1052.51, -30.16) * mm, "end": v(-1052.51, -35.01) * mm});
            skLineSegment(sketch, "E122", {"start": v(-1052.51, -35.01) * mm, "end": v(-1033.46, -35.01) * mm});
            skSolve(sketch);
        }
        {
            var Q0;
            Q0 = qSketchRegion(id + "F33", true);
            extrude(context, id + "F34", {"entities" : qUnion([Q0]), "operationType" : NewBodyOperationType.REMOVE, "oppositeDirection" : true, "depth" : 25.4 * mm, "offsetDistance" : 25.4 * mm});
        }
        {
            var Q0;
            {var subQ0=sQuery(id+"F31.wireOp",EDGE,"E109");var subQ1=sQuery(id+"F31.wireOp",EDGE,"E107");Q0=makeQuery(id+"F32.boolean.opBoolean","SPLIT",FACE,{"disambiguationData":[TD([makeQuery(id+"F1.opExtrude","SWEPT_FACE",FACE,{"disambiguationData":[OSD([sQuery(id+"F0.wireOp",EDGE,"E0.right"),sQuery(id+"F0.wireOp",EDGE,"E12"),sQuery(id+"F0.wireOp",EDGE,"E24")])]}),makeQuery(id+"F6.opExtrude","SWEPT_FACE",FACE,{"disambiguationData":[OSD([sQuery(id+"F5.wireOp",EDGE,"E42.1.0")])]}),makeQuery(id+"F16.opExtrude","CAP_FACE",FACE,{"disambiguationData":[OSD([sQuery(id+"F15.wireOp",EDGE,"E63"),sQuery(id+"F15.wireOp",EDGE,"E64"),sQuery(id+"F15.wireOp",EDGE,"E65")])],"isStart":false}),makeQuery(id+"F16.opExtrude","CAP_FACE",FACE,{"disambiguationData":[OSD([sQuery(id+"F15.wireOp",EDGE,"E66"),sQuery(id+"F15.wireOp",EDGE,"E67"),sQuery(id+"F15.wireOp",EDGE,"E68")])],"isStart":false}),makeQuery(id+"F18.opExtrude","SWEPT_FACE",FACE,{"disambiguationData":[OSD([sQuery(id+"F17.wireOp",EDGE,"E74")])]}),makeQuery(id+"F32.opExtrude","CAP_FACE",FACE,{"disambiguationData":[OSD([subQ1,sQuery(id+"F31.wireOp",EDGE,"E108"),subQ0,sQuery(id+"F31.wireOp",EDGE,"E110"),sQuery(id+"F31.wireOp",EDGE,"E111"),sQuery(id+"F31.wireOp",EDGE,"E112")])],"isStart":false}),makeQuery(id+"F32.opExtrude","SWEPT_FACE",FACE,{"disambiguationData":[OSD([subQ0])]})])],"derivedFrom":makeQuery(id+"F32.opExtrude","SWEPT_FACE",FACE,{"disambiguationData":[OSD([subQ1])]})});}
            var sketch = newSketch(context, id + "F35", { "sketchPlane" : qUnion([Q0])});
            skLineSegment(sketch, "E123", {"start": v(-35.01, -1033.46) * mm, "end": v(-30.16, -1038.31) * mm});
            skLineSegment(sketch, "E124", {"start": v(-30.16, -1038.31) * mm, "end": v(-30.16, -1052.51) * mm});
            skLineSegment(sketch, "E125", {"start": v(-30.16, -1052.51) * mm, "end": v(-35.01, -1052.51) * mm});
            skLineSegment(sketch, "E126", {"start": v(-35.01, -1052.51) * mm, "end": v(-35.01, -1033.46) * mm});
            skSolve(sketch);
        }
        {
            var Q0;
            Q0 = qSketchRegion(id + "F35", true);
            extrude(context, id + "F36", {"entities" : qUnion([Q0]), "operationType" : NewBodyOperationType.REMOVE, "oppositeDirection" : true, "depth" : 25.4 * mm, "offsetDistance" : 25.4 * mm});
        }
        {
            var Q0;
            {var subQ0=sQuery(id+"F31.wireOp",EDGE,"E112");var subQ1=sQuery(id+"F31.wireOp",EDGE,"E111");Q0=makeQuery(id+"F32.boolean.opBoolean","SPLIT",FACE,{"disambiguationData":[TD([makeQuery(id+"F1.opExtrude","SWEPT_FACE",FACE,{"disambiguationData":[OSD([sQuery(id+"F0.wireOp",EDGE,"E0.bottom"),sQuery(id+"F0.wireOp",EDGE,"E21"),sQuery(id+"F0.wireOp",EDGE,"E25")])]}),makeQuery(id+"F6.opExtrude","SWEPT_FACE",FACE,{"disambiguationData":[OSD([sQuery(id+"F5.wireOp",EDGE,"E40")])]}),makeQuery(id+"F8.opExtrude","SWEPT_FACE",FACE,{"disambiguationData":[OSD([sQuery(id+"F7.wireOp",EDGE,"E48")])]}),makeQuery(id+"F32.opExtrude","CAP_FACE",FACE,{"disambiguationData":[OSD([sQuery(id+"F31.wireOp",EDGE,"E107"),sQuery(id+"F31.wireOp",EDGE,"E108"),sQuery(id+"F31.wireOp",EDGE,"E109"),sQuery(id+"F31.wireOp",EDGE,"E110"),subQ1,subQ0])],"isStart":false}),makeQuery(id+"F32.opExtrude","SWEPT_FACE",FACE,{"disambiguationData":[OSD([subQ0])]})])],"derivedFrom":makeQuery(id+"F32.opExtrude","SWEPT_FACE",FACE,{"disambiguationData":[OSD([subQ1])]})});}
            var sketch = newSketch(context, id + "F37", { "sketchPlane" : qUnion([Q0])});
            skLineSegment(sketch, "E127", {"start": v(1033.46, 35.01) * mm, "end": v(1038.31, 30.16) * mm});
            skLineSegment(sketch, "E128", {"start": v(1038.31, 30.16) * mm, "end": v(1052.51, 30.16) * mm});
            skLineSegment(sketch, "E129", {"start": v(1052.51, 30.16) * mm, "end": v(1052.51, 35.01) * mm});
            skLineSegment(sketch, "E130", {"start": v(1052.51, 35.01) * mm, "end": v(1033.46, 35.01) * mm});
            skSolve(sketch);
        }
        {
            var Q0;
            Q0 = qSketchRegion(id + "F37", true);
            extrude(context, id + "F38", {"entities" : qUnion([Q0]), "operationType" : NewBodyOperationType.REMOVE, "oppositeDirection" : true, "depth" : 25.4 * mm, "offsetDistance" : 25.4 * mm});
        }
        {
            var Q0;
            {var subQ0=sQuery(id+"F31.wireOp",EDGE,"E118");var subQ1=sQuery(id+"F31.wireOp",EDGE,"E117");Q0=makeQuery(id+"F32.boolean.opBoolean","SPLIT",FACE,{"disambiguationData":[TD([makeQuery(id+"F1.opExtrude","SWEPT_FACE",FACE,{"disambiguationData":[OSD([sQuery(id+"F0.wireOp",EDGE,"E0.left"),sQuery(id+"F0.wireOp",EDGE,"E16"),sQuery(id+"F0.wireOp",EDGE,"E20")])]}),makeQuery(id+"F6.opExtrude","SWEPT_FACE",FACE,{"disambiguationData":[OSD([sQuery(id+"F5.wireOp",EDGE,"E39")])]}),makeQuery(id+"F8.opExtrude","CAP_FACE",FACE,{"disambiguationData":[OSD([sQuery(id+"F7.wireOp",EDGE,"E43"),sQuery(id+"F7.wireOp",EDGE,"E44"),sQuery(id+"F7.wireOp",EDGE,"E45")])],"isStart":false}),makeQuery(id+"F8.opExtrude","CAP_FACE",FACE,{"disambiguationData":[OSD([sQuery(id+"F7.wireOp",EDGE,"E46"),sQuery(id+"F7.wireOp",EDGE,"E47"),sQuery(id+"F7.wireOp",EDGE,"E48")])],"isStart":false}),makeQuery(id+"F10.opExtrude","SWEPT_FACE",FACE,{"disambiguationData":[OSD([sQuery(id+"F9.wireOp",EDGE,"E51")])]}),makeQuery(id+"F32.opExtrude","CAP_FACE",FACE,{"disambiguationData":[OSD([sQuery(id+"F31.wireOp",EDGE,"E113"),sQuery(id+"F31.wireOp",EDGE,"E114"),sQuery(id+"F31.wireOp",EDGE,"E115"),sQuery(id+"F31.wireOp",EDGE,"E116"),subQ1,subQ0])],"isStart":false}),makeQuery(id+"F32.opExtrude","SWEPT_FACE",FACE,{"disambiguationData":[OSD([subQ0])]})])],"derivedFrom":makeQuery(id+"F32.opExtrude","SWEPT_FACE",FACE,{"disambiguationData":[OSD([subQ1])]})});}
            var sketch = newSketch(context, id + "F39", { "sketchPlane" : qUnion([Q0])});
            skLineSegment(sketch, "E131", {"start": v(30.16, 1038.31) * mm, "end": v(30.16, 1052.51) * mm});
            skLineSegment(sketch, "E132", {"start": v(30.16, 1052.51) * mm, "end": v(35.01, 1052.51) * mm});
            skLineSegment(sketch, "E133", {"start": v(35.01, 1052.51) * mm, "end": v(35.01, 1033.46) * mm});
            skLineSegment(sketch, "E134", {"start": v(35.01, 1033.46) * mm, "end": v(30.16, 1038.31) * mm});
            skSolve(sketch);
        }
        {
            var Q0;
            Q0 = qSketchRegion(id + "F39", true);
            extrude(context, id + "F40", {"entities" : qUnion([Q0]), "operationType" : NewBodyOperationType.REMOVE, "oppositeDirection" : true, "depth" : 25.4 * mm, "offsetDistance" : 25.4 * mm});
        }
        {
            var Q0;
            Q0=makeQuery(id+"F1.opExtrude","CAP_FACE",FACE,{"disambiguationData":[OSD([sQuery(id+"F0.wireOp",EDGE,"E0.bottom"),sQuery(id+"F0.wireOp",EDGE,"E0.top"),sQuery(id+"F0.wireOp",EDGE,"E0.left"),sQuery(id+"F0.wireOp",EDGE,"E0.right"),sQuery(id+"F0.wireOp",EDGE,"E1.0"),sQuery(id+"F0.wireOp",EDGE,"E1.1"),sQuery(id+"F0.wireOp",EDGE,"E1.2"),sQuery(id+"F0.wireOp",EDGE,"E1.3"),sQuery(id+"F0.wireOp",EDGE,"E10"),sQuery(id+"F0.wireOp",EDGE,"E11"),sQuery(id+"F0.wireOp",EDGE,"E12"),sQuery(id+"F0.wireOp",EDGE,"E13"),sQuery(id+"F0.wireOp",EDGE,"E14"),sQuery(id+"F0.wireOp",EDGE,"E15"),sQuery(id+"F0.wireOp",EDGE,"E16"),sQuery(id+"F0.wireOp",EDGE,"E17"),sQuery(id+"F0.wireOp",EDGE,"E18"),sQuery(id+"F0.wireOp",EDGE,"E19"),sQuery(id+"F0.wireOp",EDGE,"E20"),sQuery(id+"F0.wireOp",EDGE,"E21"),sQuery(id+"F0.wireOp",EDGE,"E22"),sQuery(id+"F0.wireOp",EDGE,"E23"),sQuery(id+"F0.wireOp",EDGE,"E24"),sQuery(id+"F0.wireOp",EDGE,"E25")])],"isStart":true});
            var sketch = newSketch(context, id + "F41", { "sketchPlane" : qUnion([Q0])});
            skLineSegment(sketch, "E135.bottom", {"start": v(26.99, 26.99) * mm, "end": v(-26.99, 26.99) * mm});
            skLineSegment(sketch, "E135.top", {"start": v(26.99, -26.99) * mm, "end": v(-26.99, -26.99) * mm});
            skLineSegment(sketch, "E135.left", {"start": v(26.99, 26.99) * mm, "end": v(26.99, -26.99) * mm});
            skLineSegment(sketch, "E135.right", {"start": v(-26.99, 26.99) * mm, "end": v(-26.99, -26.99) * mm});
            skPoint(sketch, "E135.middle", {"position": v(0, 0) * mm});
            skSolve(sketch);
        }
        {
            var Q0;
            Q0 = qSketchRegion(id + "F41", true);
            extrude(context, id + "F42", {"entities" : qUnion([Q0]), "operationType" : NewBodyOperationType.REMOVE, "oppositeDirection" : true, "depth" : 1239.52 * mm, "offsetDistance" : 25.4 * mm});
        }
        {
            var Q0;
            {var subQ10=sQuery(id+"F0.wireOp",EDGE,"E24");var subQ13=sQuery(id+"F0.wireOp",EDGE,"E12");var subQ14=sQuery(id+"F0.wireOp",EDGE,"E0.right");var subQ18=makeQuery(id+"F3.opExtrude","SWEPT_FACE",FACE,{"disambiguationData":[OSD([sQuery(id+"F2.wireOp",EDGE,"E29")])]});Q0=makeQuery(id+"F36.boolean.opBoolean","MERGE",FACE,{"derivedFrom":[makeQuery(id+"F32.boolean.opBoolean","SPLIT",FACE,{"disambiguationData":[TD([makeQuery(id+"F16.opExtrude","SWEPT_FACE",FACE,{"disambiguationData":[OSD([sQuery(id+"F15.wireOp",EDGE,"E68")])]})])],"derivedFrom":makeQuery(id+"F20.boolean.opBoolean","MERGE",FACE,{"derivedFrom":[makeQuery(id+"F3.boolean.opBoolean","SPLIT",FACE,{"disambiguationData":[TD([subQ18])],"derivedFrom":makeQuery(id+"F1.opExtrude","SWEPT_FACE",FACE,{"disambiguationData":[OSD([subQ14,subQ13,subQ10])]})})],"fromTools":[makeQuery(id+"F20.opExtrude","SWEPT_FACE",FACE,{"disambiguationData":[OSD([sQuery(id+"F19.wireOp",EDGE,"E75")])]})]})})],"fromTools":[makeQuery(id+"F36.opExtrude","SWEPT_FACE",FACE,{"disambiguationData":[OSD([sQuery(id+"F35.wireOp",EDGE,"E124")])]})]});}
            var sketch = newSketch(context, id + "F43", { "sketchPlane" : qUnion([Q0])});
            skCircle(sketch, "E136", {"center": v(-1059.66, 11.11) * mm, "radius": 10.32 * mm});
            skSolve(sketch);
        }
        {
            var Q0;
            Q0 = qSketchRegion(id + "F43", true);
            extrude(context, id + "F44", {"entities" : qUnion([Q0]), "operationType" : NewBodyOperationType.REMOVE, "oppositeDirection" : true, "depth" : 89.66 * mm, "offsetDistance" : 25.4 * mm});
        }
        {
            var Q0;
            {var subQ1=makeQuery(id+"F3.opExtrude","SWEPT_FACE",FACE,{"disambiguationData":[OSD([sQuery(id+"F2.wireOp",EDGE,"E27"),sQuery(id+"F2.wireOp",EDGE,"E31")])]});var subQ8=sQuery(id+"F0.wireOp",EDGE,"E24");var subQ12=sQuery(id+"F0.wireOp",EDGE,"E12");var subQ13=sQuery(id+"F0.wireOp",EDGE,"E0.right");Q0=makeQuery(id+"F30.boolean.opBoolean","MERGE",FACE,{"derivedFrom":[makeQuery(id+"F22.boolean.opBoolean","SPLIT",FACE,{"disambiguationData":[TD([makeQuery(id+"F16.opExtrude","SWEPT_FACE",FACE,{"disambiguationData":[OSD([sQuery(id+"F15.wireOp",EDGE,"E64")])]})])],"derivedFrom":makeQuery(id+"F3.boolean.opBoolean","SPLIT",FACE,{"disambiguationData":[TD([subQ1])],"derivedFrom":makeQuery(id+"F1.opExtrude","SWEPT_FACE",FACE,{"disambiguationData":[OSD([subQ13,subQ12,subQ8])]})})})],"fromTools":[makeQuery(id+"F30.opExtrude","SWEPT_FACE",FACE,{"disambiguationData":[OSD([sQuery(id+"F29.wireOp",EDGE,"E103")])]})]});}
            var sketch = newSketch(context, id + "F45", { "sketchPlane" : qUnion([Q0])});
            skCircle(sketch, "E137", {"center": v(-111.13, 0) * mm, "radius": 10.32 * mm});
            skSolve(sketch);
        }
        {
            var Q0;
            Q0 = qSketchRegion(id + "F45", true);
            extrude(context, id + "F46", {"entities" : qUnion([Q0]), "operationType" : NewBodyOperationType.REMOVE, "oppositeDirection" : true, "depth" : 179.83 * mm, "offsetDistance" : 25.4 * mm});
        }
    });
